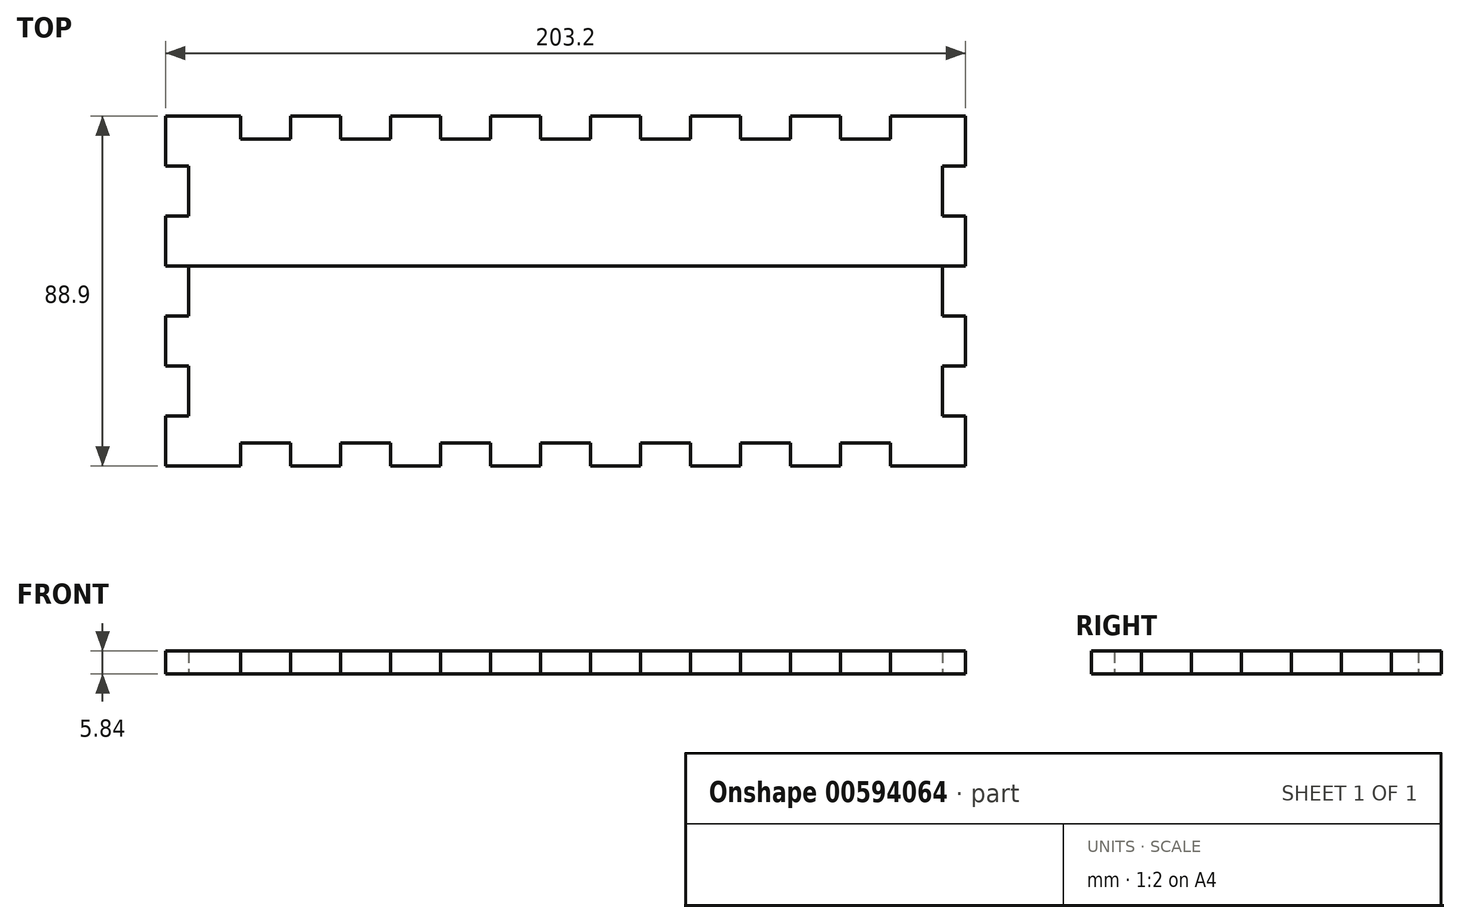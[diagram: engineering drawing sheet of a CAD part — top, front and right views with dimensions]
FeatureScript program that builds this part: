
annotation { "Feature Type Name" : "Feature", "Feature Type Description" : "" }
export const myFeature = defineFeature(function(context is Context, id is Id, definition is map)
    precondition{}
    {
        {
            var Q0;
            Q0=qCreatedBy(makeId("Top.planeOp"),FACE);
            var sketch = newSketch(context, id + "F0", { "sketchPlane" : qUnion([Q0])});
            skLineSegment(sketch, "E0.bottom", {"start": v(0, 0) * mm, "end": v(19.05, 0) * mm});
            skLineSegment(sketch, "E0.left", {"start": v(0, 0) * mm, "end": v(0, -12.7) * mm});
            skLineSegment(sketch, "E1", {"start": v(19.05, 0) * mm, "end": v(19.05, -5.84) * mm});
            skLineSegment(sketch, "E2", {"start": v(19.05, -5.84) * mm, "end": v(31.75, -5.84) * mm});
            skLineSegment(sketch, "E3", {"start": v(31.75, -5.84) * mm, "end": v(31.75, 0) * mm});
            skLineSegment(sketch, "E4", {"start": v(31.75, 0) * mm, "end": v(44.45, 0) * mm});
            skLineSegment(sketch, "E5", {"start": v(44.45, 0) * mm, "end": v(44.45, -5.84) * mm});
            skLineSegment(sketch, "E6", {"start": v(44.45, -5.84) * mm, "end": v(57.15, -5.84) * mm});
            skLineSegment(sketch, "E7", {"start": v(57.15, -5.84) * mm, "end": v(57.15, 0) * mm});
            skLineSegment(sketch, "E8", {"start": v(57.15, 0) * mm, "end": v(69.85, 0) * mm});
            skLineSegment(sketch, "E9", {"start": v(69.85, 0) * mm, "end": v(69.85, -5.84) * mm});
            skLineSegment(sketch, "E10", {"start": v(69.85, -5.84) * mm, "end": v(82.55, -5.84) * mm});
            skLineSegment(sketch, "E11", {"start": v(82.55, -5.84) * mm, "end": v(82.55, 0) * mm});
            skLineSegment(sketch, "E12.trimOffspring", {"start": v(82.55, 0) * mm, "end": v(95.25, 0) * mm});
            skLineSegment(sketch, "E13", {"start": v(95.25, 0) * mm, "end": v(95.25, -5.84) * mm});
            skLineSegment(sketch, "E14", {"start": v(95.25, -5.84) * mm, "end": v(107.95, -5.84) * mm});
            skLineSegment(sketch, "E15", {"start": v(107.95, -5.84) * mm, "end": v(107.95, 0) * mm});
            skLineSegment(sketch, "E16", {"start": v(107.95, 0) * mm, "end": v(120.65, 0) * mm});
            skLineSegment(sketch, "E17", {"start": v(120.65, 0) * mm, "end": v(120.65, -5.84) * mm});
            skLineSegment(sketch, "E18", {"start": v(120.65, -5.84) * mm, "end": v(133.35, -5.84) * mm});
            skLineSegment(sketch, "E19", {"start": v(133.35, -5.84) * mm, "end": v(133.35, 0) * mm});
            skLineSegment(sketch, "E20", {"start": v(133.35, 0) * mm, "end": v(146.05, 0) * mm});
            skLineSegment(sketch, "E21", {"start": v(146.05, 0) * mm, "end": v(146.05, -5.84) * mm});
            skLineSegment(sketch, "E22", {"start": v(146.05, -5.84) * mm, "end": v(158.75, -5.84) * mm});
            skLineSegment(sketch, "E23", {"start": v(158.75, -5.84) * mm, "end": v(158.75, 0) * mm});
            skLineSegment(sketch, "E24.trimOffspring", {"start": v(158.75, 0) * mm, "end": v(171.45, 0) * mm});
            skLineSegment(sketch, "E25", {"start": v(171.45, 0) * mm, "end": v(171.45, -5.84) * mm});
            skLineSegment(sketch, "E26", {"start": v(171.45, -5.84) * mm, "end": v(184.15, -5.84) * mm});
            skLineSegment(sketch, "E27", {"start": v(184.15, -5.84) * mm, "end": v(184.15, 0) * mm});
            skLineSegment(sketch, "E28.trimOffspring", {"start": v(184.15, 0) * mm, "end": v(203.2, 0) * mm});
            skLineSegment(sketch, "E29", {"start": v(0, -12.7) * mm, "end": v(5.84, -12.7) * mm});
            skLineSegment(sketch, "E30", {"start": v(5.84, -12.7) * mm, "end": v(5.84, -25.4) * mm});
            skLineSegment(sketch, "E31", {"start": v(5.84, -25.4) * mm, "end": v(0, -25.4) * mm});
            skLineSegment(sketch, "E32", {"start": v(0, -25.4) * mm, "end": v(0, -38.1) * mm});
            skLineSegment(sketch, "E33", {"start": v(0, -38.1) * mm, "end": v(5.84, -38.1) * mm});
            skLineSegment(sketch, "E34", {"start": v(5.84, -38.1) * mm, "end": v(5.84, -50.8) * mm});
            skLineSegment(sketch, "E35", {"start": v(5.84, -50.8) * mm, "end": v(0, -50.8) * mm});
            skLineSegment(sketch, "E36", {"start": v(0, -50.8) * mm, "end": v(0, -63.5) * mm});
            skLineSegment(sketch, "E37", {"start": v(0, -63.5) * mm, "end": v(5.84, -63.5) * mm});
            skLineSegment(sketch, "E38", {"start": v(5.84, -63.5) * mm, "end": v(5.84, -76.2) * mm});
            skLineSegment(sketch, "E39", {"start": v(5.84, -76.2) * mm, "end": v(0, -76.2) * mm});
            skLineSegment(sketch, "E40.trimOffspring", {"start": v(0, -76.2) * mm, "end": v(0, -88.9) * mm});
            skLineSegment(sketch, "E41", {"start": v(101.6, -5.84) * mm, "end": v(101.6, -30.32) * mm, "construction": true});
            skLineSegment(sketch, "E42", {"start": v(5.84, -44.45) * mm, "end": v(28.65, -44.45) * mm, "construction": true});
            skLineSegment(sketch, "E43.MirrorCS", {"start": v(197.36, -12.7) * mm, "end": v(197.36, -25.4) * mm});
            skLineSegment(sketch, "E44.MirrorCS", {"start": v(203.2, 0) * mm, "end": v(203.2, -12.7) * mm});
            skLineSegment(sketch, "E45.MirrorCS", {"start": v(203.2, -12.7) * mm, "end": v(197.36, -12.7) * mm});
            skLineSegment(sketch, "E46.MirrorCS", {"start": v(203.2, -25.4) * mm, "end": v(203.2, -38.1) * mm});
            skLineSegment(sketch, "E47.MirrorCS", {"start": v(197.36, -25.4) * mm, "end": v(203.2, -25.4) * mm});
            skLineSegment(sketch, "E48.MirrorCS", {"start": v(203.2, -38.1) * mm, "end": v(197.36, -38.1) * mm});
            skLineSegment(sketch, "E49.MirrorCS", {"start": v(197.36, -38.1) * mm, "end": v(197.36, -50.8) * mm});
            skLineSegment(sketch, "E50.MirrorCS", {"start": v(197.36, -50.8) * mm, "end": v(203.2, -50.8) * mm});
            skLineSegment(sketch, "E51.MirrorCS", {"start": v(203.2, -50.8) * mm, "end": v(203.2, -63.5) * mm});
            skLineSegment(sketch, "E52.MirrorCS", {"start": v(203.2, -63.5) * mm, "end": v(197.36, -63.5) * mm});
            skLineSegment(sketch, "E53.MirrorCS", {"start": v(197.36, -63.5) * mm, "end": v(197.36, -76.2) * mm});
            skLineSegment(sketch, "E54.MirrorCS", {"start": v(197.36, -76.2) * mm, "end": v(203.2, -76.2) * mm});
            skLineSegment(sketch, "E55.MirrorCS", {"start": v(203.2, -76.2) * mm, "end": v(203.2, -88.9) * mm});
            skLineSegment(sketch, "E56.MirrorCS", {"start": v(0, -88.9) * mm, "end": v(19.05, -88.9) * mm});
            skLineSegment(sketch, "E57.MirrorCS", {"start": v(19.05, -88.9) * mm, "end": v(19.05, -83.06) * mm});
            skLineSegment(sketch, "E58.MirrorCS", {"start": v(19.05, -83.06) * mm, "end": v(31.75, -83.06) * mm});
            skLineSegment(sketch, "E59.MirrorCS", {"start": v(31.75, -83.06) * mm, "end": v(31.75, -88.9) * mm});
            skLineSegment(sketch, "E60.MirrorCS", {"start": v(31.75, -88.9) * mm, "end": v(44.45, -88.9) * mm});
            skLineSegment(sketch, "E61.MirrorCS", {"start": v(44.45, -88.9) * mm, "end": v(44.45, -83.06) * mm});
            skLineSegment(sketch, "E62.MirrorCS", {"start": v(44.45, -83.06) * mm, "end": v(57.15, -83.06) * mm});
            skLineSegment(sketch, "E63.MirrorCS", {"start": v(57.15, -83.06) * mm, "end": v(57.15, -88.9) * mm});
            skLineSegment(sketch, "E64.MirrorCS", {"start": v(57.15, -88.9) * mm, "end": v(69.85, -88.9) * mm});
            skLineSegment(sketch, "E65.MirrorCS", {"start": v(69.85, -88.9) * mm, "end": v(69.85, -83.06) * mm});
            skLineSegment(sketch, "E66.MirrorCS", {"start": v(69.85, -83.06) * mm, "end": v(82.55, -83.06) * mm});
            skLineSegment(sketch, "E67.MirrorCS", {"start": v(82.55, -83.06) * mm, "end": v(82.55, -88.9) * mm});
            skLineSegment(sketch, "E68.MirrorCS", {"start": v(82.55, -88.9) * mm, "end": v(95.25, -88.9) * mm});
            skLineSegment(sketch, "E69.MirrorCS", {"start": v(95.25, -88.9) * mm, "end": v(95.25, -83.06) * mm});
            skLineSegment(sketch, "E70.MirrorCS", {"start": v(95.25, -83.06) * mm, "end": v(107.95, -83.06) * mm});
            skLineSegment(sketch, "E71.MirrorCS", {"start": v(107.95, -83.06) * mm, "end": v(107.95, -88.9) * mm});
            skLineSegment(sketch, "E72.MirrorCS", {"start": v(107.95, -88.9) * mm, "end": v(120.65, -88.9) * mm});
            skLineSegment(sketch, "E73.MirrorCS", {"start": v(120.65, -88.9) * mm, "end": v(120.65, -83.06) * mm});
            skLineSegment(sketch, "E74.MirrorCS", {"start": v(120.65, -83.06) * mm, "end": v(133.35, -83.06) * mm});
            skLineSegment(sketch, "E75.MirrorCS", {"start": v(133.35, -83.06) * mm, "end": v(133.35, -88.9) * mm});
            skLineSegment(sketch, "E76.MirrorCS", {"start": v(133.35, -88.9) * mm, "end": v(146.05, -88.9) * mm});
            skLineSegment(sketch, "E77.MirrorCS", {"start": v(146.05, -88.9) * mm, "end": v(146.05, -83.06) * mm});
            skLineSegment(sketch, "E78.MirrorCS", {"start": v(146.05, -83.06) * mm, "end": v(158.75, -83.06) * mm});
            skLineSegment(sketch, "E79.MirrorCS", {"start": v(158.75, -83.06) * mm, "end": v(158.75, -88.9) * mm});
            skLineSegment(sketch, "E80.MirrorCS", {"start": v(158.75, -88.9) * mm, "end": v(171.45, -88.9) * mm});
            skLineSegment(sketch, "E81.MirrorCS", {"start": v(171.45, -88.9) * mm, "end": v(171.45, -83.06) * mm});
            skLineSegment(sketch, "E82.MirrorCS", {"start": v(171.45, -83.06) * mm, "end": v(184.15, -83.06) * mm});
            skLineSegment(sketch, "E83.MirrorCS", {"start": v(184.15, -83.06) * mm, "end": v(184.15, -88.9) * mm});
            skLineSegment(sketch, "E84.MirrorCS", {"start": v(184.15, -88.9) * mm, "end": v(203.2, -88.9) * mm});
            skLineSegment(sketch, "E85", {"start": v(5.84, -38.1) * mm, "end": v(197.36, -38.1) * mm});
            skSolve(sketch);
        }
        {
            var Q0;
            Q0=makeQuery(id+"F0.imprint","IMPRINT",FACE,{"disambiguationData":[TD([[makeQuery(id+"F0.imprint","IMPRINT",EDGE,{"derivedFrom":sQuery(id+"F0.wireOp",EDGE,"E0.bottom")}),-1.0]])]});
            extrude(context, id + "F1", {"entities" : qUnion([Q0]), "depth" : 5.84 * mm, "offsetDistance" : 25.4 * mm});
        }
        {
            var Q0;
            Q0=makeQuery(id+"F0.imprint","IMPRINT",FACE,{"disambiguationData":[TD([[makeQuery(id+"F0.imprint","IMPRINT",EDGE,{"derivedFrom":sQuery(id+"F0.wireOp",EDGE,"E34")}),1.0]])]});
            extrude(context, id + "F2", {"entities" : qUnion([Q0]), "depth" : 5.84 * mm, "offsetDistance" : 25.4 * mm});
        }
    });
